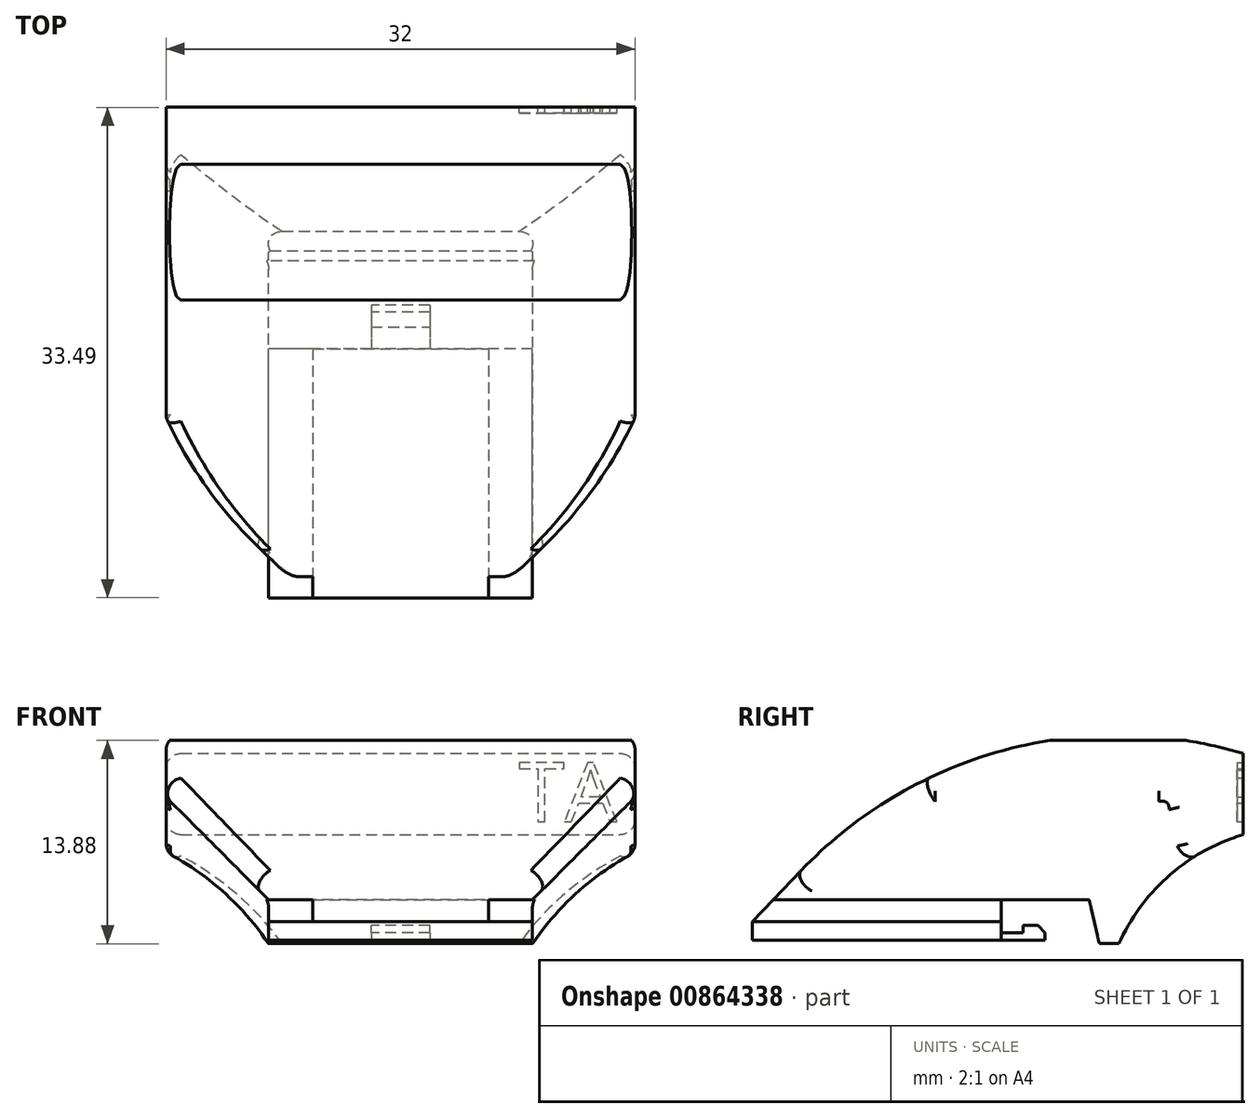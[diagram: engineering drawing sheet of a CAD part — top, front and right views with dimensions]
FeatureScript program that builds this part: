
annotation { "Feature Type Name" : "Feature", "Feature Type Description" : "" }
export const myFeature = defineFeature(function(context is Context, id is Id, definition is map)
    precondition{}
    {
        {
            var Q0;
            Q0=qCreatedBy(makeId("Front.planeOp"),FACE);
            var sketch = newSketch(context, id + "F0", { "sketchPlane" : qUnion([Q0])});
            skLineSegment(sketch, "E0.bottom", {"start": v(9, 0.63) * mm, "end": v(-9, 0.63) * mm});
            skLineSegment(sketch, "E0.top", {"start": v(9, -0.62) * mm, "end": v(-9, -0.62) * mm});
            skLineSegment(sketch, "E0.left", {"start": v(9, 0.63) * mm, "end": v(9, -0.62) * mm});
            skLineSegment(sketch, "E0.right", {"start": v(-9, 0.63) * mm, "end": v(-9, -0.62) * mm});
            skPoint(sketch, "E0.middle", {"position": v(0, 0) * mm});
            skSolve(sketch);
        }
        {
            var Q0;
            Q0=makeQuery(id+"F0.imprint","IMPRINT",FACE,{"disambiguationData":[TD([[makeQuery(id+"F0.imprint","IMPRINT",EDGE,{"derivedFrom":sQuery(id+"F0.wireOp",EDGE,"E0.bottom")}),1.0]])]});
            extrude(context, id + "F1", {"entities" : qUnion([Q0]), "depth" : 17 * mm, "offsetDistance" : 25 * mm});
        }
        {
            var Q0;
            Q0=makeQuery(id+"F1.opExtrude","SWEPT_FACE",FACE,{"disambiguationData":[OSD([sQuery(id+"F0.wireOp",EDGE,"E0.bottom")])]});
            var sketch = newSketch(context, id + "F2", { "sketchPlane" : qUnion([Q0])});
            skLineSegment(sketch, "E1", {"start": v(-9, 0) * mm, "end": v(-6, 0) * mm});
            skLineSegment(sketch, "E2", {"start": v(9, 0) * mm, "end": v(6, 0) * mm});
            skLineSegment(sketch, "E3", {"start": v(-6, 0) * mm, "end": v(-6, -17) * mm});
            skLineSegment(sketch, "E4", {"start": v(6, 0) * mm, "end": v(6, -17) * mm});
            skSolve(sketch);
        }
        {
            var Q0;
            {var subQ0=sQuery(id+"F2.wireOp",EDGE,"E3");Q0=makeQuery(id+"F2.imprint","IMPRINT",FACE,{"disambiguationData":[TD([[makeQuery(id+"F2.imprint","IMPRINT",EDGE,{"derivedFrom":subQ0}),1.0]])]});}
            extrude(context, id + "F3", {"entities" : qUnion([Q0]), "operationType" : NewBodyOperationType.ADD, "depth" : 1.5 * mm, "offsetDistance" : 25 * mm});
        }
        {
            var Q0;
            {var subQ0=sQuery(id+"F0.wireOp",EDGE,"E0.bottom");var subQ1=makeQuery(id+"F1.opExtrude","CAP_EDGE",EDGE,{"disambiguationData":[OSD([subQ0])],"isStart":true});Q0=makeQuery(id+"F3.boolean.opBoolean","MERGE",FACE,{"derivedFrom":[makeQuery(id+"F1.opExtrude","CAP_FACE",FACE,{"disambiguationData":[OSD([subQ0,sQuery(id+"F0.wireOp",EDGE,"E0.top"),sQuery(id+"F0.wireOp",EDGE,"E0.left"),sQuery(id+"F0.wireOp",EDGE,"E0.right")])],"isStart":true}),makeQuery(id+"F3.opExtrude","SWEPT_FACE",FACE,{"disambiguationData":[OSD([subQ0]),TDD([makeQuery(id+"F2.imprint","IMPRINT",EDGE,{"disambiguationData":[TD([[makeQuery(id+"F2.imprint","INTERSECT",VERTEX,{"derivedFrom":[subQ1,sQuery(id+"F2.wireOp",EDGE,"E1"),sQuery(id+"F2.wireOp",EDGE,"E3")]}),1.0]])],"derivedFrom":subQ1})])]})]});}
            var sketch = newSketch(context, id + "F4", { "sketchPlane" : qUnion([Q0])});
            skLineSegment(sketch, "E5", {"start": v(-9, -0.62) * mm, "end": v(0, -0.62) * mm});
            skLineSegment(sketch, "E6", {"start": v(-2, 0.38) * mm, "end": v(-2, -0.62) * mm});
            skLineSegment(sketch, "E7", {"start": v(2, 0.38) * mm, "end": v(2, -0.62) * mm});
            skLineSegment(sketch, "E8", {"start": v(-2, 0.38) * mm, "end": v(2, 0.38) * mm});
            skSolve(sketch);
        }
        {
            var Q0;
            {var subQ1=sQuery(id+"F4.wireOp",EDGE,"E6");Q0=makeQuery(id+"F4.imprint","IMPRINT",FACE,{"disambiguationData":[TD([[makeQuery(id+"F4.imprint","IMPRINT",EDGE,{"derivedFrom":subQ1}),1.0]])]});}
            extrude(context, id + "F5", {"entities" : qUnion([Q0]), "operationType" : NewBodyOperationType.ADD, "depth" : 3 * mm, "offsetDistance" : 25 * mm});
        }
        {
            var Q0;
            Q0=makeQuery(id+"F5.opExtrude","SWEPT_FACE",FACE,{"disambiguationData":[OSD([sQuery(id+"F4.wireOp",EDGE,"E8")])]});
            var sketch = newSketch(context, id + "F6", { "sketchPlane" : qUnion([Q0])});
            skLineSegment(sketch, "E9", {"start": v(-2, 1.5) * mm, "end": v(2, 1.5) * mm});
            skSolve(sketch);
        }
        {
            var Q0;
            {var subQ0=sQuery(id+"F6.wireOp",EDGE,"E9");Q0=makeQuery(id+"F6.imprint","IMPRINT",FACE,{"disambiguationData":[TD([[makeQuery(id+"F6.imprint","IMPRINT",EDGE,{"derivedFrom":subQ0}),-1.0]])]});}
            extrude(context, id + "F7", {"entities" : qUnion([Q0]), "operationType" : NewBodyOperationType.REMOVE, "oppositeDirection" : true, "depth" : .5 * mm, "offsetDistance" : 25 * mm});
        }
        {
            var Q0;
            Q0=makeQuery(id+"F5.opExtrude","SWEPT_FACE",FACE,{"disambiguationData":[OSD([sQuery(id+"F4.wireOp",EDGE,"E7")])]});
            var sketch = newSketch(context, id + "F8", { "sketchPlane" : qUnion([Q0])});
            skLineSegment(sketch, "E10", {"start": v(-1.5, -0.12) * mm, "end": v(-3, -0.12) * mm});
            skLineSegment(sketch, "E11", {"start": v(-1.5, 0.38) * mm, "end": v(-2.5, 0.38) * mm});
            skLineSegment(sketch, "E12", {"start": v(-3, -0.12) * mm, "end": v(-2.5, 0.38) * mm});
            skSolve(sketch);
        }
        {
            var Q0;
            {var subQ0=sQuery(id+"F8.wireOp",EDGE,"E12");Q0=makeQuery(id+"F8.imprint","IMPRINT",FACE,{"disambiguationData":[TD([[makeQuery(id+"F8.imprint","IMPRINT",EDGE,{"derivedFrom":subQ0}),1.0]])]});}
            extrude(context, id + "F9", {"entities" : qUnion([Q0]), "operationType" : NewBodyOperationType.REMOVE, "oppositeDirection" : true, "depth" : 25 * mm, "offsetDistance" : 25 * mm});
        }
        {
            var Q0;
            Q0=makeQuery(id+"F3.opExtrude","CAP_FACE",FACE,{"disambiguationData":[OSD([sQuery(id+"F0.wireOp",EDGE,"E0.bottom"),sQuery(id+"F2.wireOp",EDGE,"E3"),sQuery(id+"F2.wireOp",EDGE,"E4")])],"isStart":false});
            var sketch = newSketch(context, id + "F10", { "sketchPlane" : qUnion([Q0])});
            skLineSegment(sketch, "E13", {"start": v(0, 0) * mm, "end": v(0, -17) * mm});
            skSolve(sketch);
        }
        {
            var Q0;
            {var subQ4=sQuery(id+"F10.wireOp",EDGE,"9KFDr5Zl-xlse-Ylvu-UwML-SPBPVxaVvAoh");Q0=makeQuery(id+"F10.imprint","IMPRINT",FACE,{"disambiguationData":[TD([[makeQuery(id+"F10.imprint","IMPRINT",EDGE,{"derivedFrom":subQ4}),-1.0]])]});}
            var Q1;
            {var subQ4=sQuery(id+"F10.wireOp",EDGE,"uYcF2vPk-5izG-vbNe-kog8-wCf3jsevN1tl");Q1=makeQuery(id+"F10.imprint","IMPRINT",FACE,{"disambiguationData":[TD([[makeQuery(id+"F10.imprint","IMPRINT",EDGE,{"derivedFrom":subQ4}),-1.0]])]});}
            var Q2;
            {var subQ1=sQuery(id+"F10.wireOp",EDGE,"418b0c24-5611-44d3-8d25-239d1beeb747.sketch_text.stroke-0");Q2=makeQuery(id+"F10.imprint","IMPRINT",FACE,{"disambiguationData":[TD([[makeQuery(id+"F10.imprint","IMPRINT",EDGE,{"derivedFrom":subQ1}),-1.0]])]});}
            var Q3;
            Q3=makeQuery(id+"F10.imprint","IMPRINT",FACE,{"disambiguationData":[TD([[makeQuery(id+"F10.imprint","IMPRINT",EDGE,{"derivedFrom":sQuery(id+"F10.wireOp",EDGE,"418b0c24-5611-44d3-8d25-239d1beeb747.sketch_text.stroke-13")}),-1.0]])]});
            var Q4;
            {var subQ0=sQuery(id+"F10.wireOp",EDGE,"418b0c24-5611-44d3-8d25-239d1beeb747.sketch_text.stroke-6");var subQ1=sQuery(id+"F10.wireOp",EDGE,"E13");var subQ2=makeQuery(id+"F10.imprint","INTERSECT",VERTEX,{"derivedFrom":[subQ1,subQ0]});Q4=makeQuery(id+"F10.imprint","IMPRINT",FACE,{"disambiguationData":[TD([[makeQuery(id+"F10.imprint","IMPRINT",EDGE,{"disambiguationData":[TD([[subQ2,-1.0]])],"derivedFrom":subQ1}),1.0]])]});}
            extrude(context, id + "F11", {"entities" : qUnion([Q0, Q1, Q2, Q3, Q4]), "operationType" : NewBodyOperationType.REMOVE, "oppositeDirection" : true, "depth" : .4 * mm, "offsetDistance" : 25 * mm});
        }
        {
            var Q0;
            {var subQ0=sQuery(id+"F10.wireOp",EDGE,"E13");Q0=makeQuery(id+"F10.imprint","IMPRINT",FACE,{"disambiguationData":[TD([[makeQuery(id+"F10.imprint","IMPRINT",EDGE,{"derivedFrom":subQ0}),-1.0]])]});}
            var Q1;
            {var subQ0=sQuery(id+"F10.wireOp",EDGE,"E13");Q1=makeQuery(id+"F10.imprint","IMPRINT",FACE,{"disambiguationData":[TD([[makeQuery(id+"F10.imprint","IMPRINT",EDGE,{"derivedFrom":subQ0}),1.0]])]});}
            var Q2;
            Q2=makeQuery(id+"F11.boolean.opBoolean","COPY",FACE,{"derivedFrom":makeQuery(id+"F11.opExtrude","CAP_FACE",FACE,{"disambiguationData":[OSD([sQuery(id+"F0.wireOp",EDGE,"E0.bottom"),sQuery(id+"F2.wireOp",EDGE,"E4"),sQuery(id+"F10.wireOp",EDGE,"E13")])],"isStart":false})});
            extrude(context, id + "F12", {"entities" : qUnion([Q0, Q1, Q2]), "operationType" : NewBodyOperationType.ADD, "depth" : 2 * mm, "offsetDistance" : 25 * mm});
        }
        {
            var Q0;
            {var subQ0=sQuery(id+"F2.wireOp",EDGE,"E3");Q0=makeQuery(id+"F12.boolean.opBoolean","MERGE",FACE,{"derivedFrom":[makeQuery(id+"F3.opExtrude","SWEPT_FACE",FACE,{"disambiguationData":[OSD([subQ0])]}),makeQuery(id+"F12.opExtrude","SWEPT_FACE",FACE,{"disambiguationData":[OSD([subQ0])]})]});}
            var sketch = newSketch(context, id + "F13", { "sketchPlane" : qUnion([Q0])});
            skLineSegment(sketch, "E14", {"start": v(13.65, 4.13) * mm, "end": v(17, 0.63) * mm});
            skSolve(sketch);
        }
        {
            var Q0;
            {var subQ0=sQuery(id+"F13.wireOp",EDGE,"E14");Q0=makeQuery(id+"F13.imprint","IMPRINT",FACE,{"disambiguationData":[TD([[makeQuery(id+"F13.imprint","IMPRINT",EDGE,{"derivedFrom":subQ0}),1.0]])]});}
            extrude(context, id + "F14", {"entities" : qUnion([Q0]), "operationType" : NewBodyOperationType.REMOVE, "oppositeDirection" : true, "depth" : 25 * mm, "offsetDistance" : 25 * mm});
        }
        {
            var Q0;
            {var subQ0=sQuery(id+"F2.wireOp",EDGE,"E3");var subQ1=sQuery(id+"F0.wireOp",EDGE,"E0.bottom");var subQ2=makeQuery(id+"F1.opExtrude","CAP_EDGE",EDGE,{"disambiguationData":[OSD([subQ1])],"isStart":true});var subQ3=sQuery(id+"F2.wireOp",EDGE,"E4");var subQ4=makeQuery(id+"F2.imprint","IMPRINT",EDGE,{"disambiguationData":[TD([[makeQuery(id+"F2.imprint","INTERSECT",VERTEX,{"derivedFrom":[subQ2,sQuery(id+"F2.wireOp",EDGE,"E1"),subQ0]}),1.0]])],"derivedFrom":subQ2});var subQ5=makeQuery(id+"F3.opExtrude","CAP_EDGE",EDGE,{"disambiguationData":[OSD([subQ1]),TDD([subQ4])],"isStart":false});var subQ7=makeQuery(id+"F10.imprint","IMPRINT",EDGE,{"disambiguationData":[TD([[makeQuery(id+"F10.imprint","INTERSECT",VERTEX,{"derivedFrom":[makeQuery(id+"F3.opExtrude","CAP_EDGE",EDGE,{"disambiguationData":[OSD([subQ3])],"isStart":false}),subQ5]}),-1.0]])],"derivedFrom":subQ5});Q0=makeQuery(id+"F12.boolean.opBoolean","MERGE",FACE,{"derivedFrom":[makeQuery(id+"F7.boolean.opBoolean","MERGE",FACE,{"derivedFrom":[makeQuery(id+"F3.boolean.opBoolean","MERGE",FACE,{"derivedFrom":[makeQuery(id+"F1.opExtrude","CAP_FACE",FACE,{"disambiguationData":[OSD([subQ1,sQuery(id+"F0.wireOp",EDGE,"E0.top"),sQuery(id+"F0.wireOp",EDGE,"E0.left"),sQuery(id+"F0.wireOp",EDGE,"E0.right")])],"isStart":true}),makeQuery(id+"F3.opExtrude","SWEPT_FACE",FACE,{"disambiguationData":[OSD([subQ1]),TDD([subQ4])]})]}),makeQuery(id+"F7.opExtrude","SWEPT_FACE",FACE,{"disambiguationData":[OSD([sQuery(id+"F4.wireOp",EDGE,"E8")])]})]}),makeQuery(id+"F12.opExtrude","SWEPT_FACE",FACE,{"disambiguationData":[OSD([subQ1]),TDD([makeQuery(id+"F10.imprint","IMPRINT",EDGE,{"disambiguationData":[TD([[makeQuery(id+"F10.imprint","INTERSECT",VERTEX,{"derivedFrom":[makeQuery(id+"F3.opExtrude","CAP_EDGE",EDGE,{"disambiguationData":[OSD([subQ0])],"isStart":false}),subQ5]}),1.0]])],"derivedFrom":subQ5}),subQ7])]}),makeQuery(id+"F12.opExtrude","SWEPT_FACE",FACE,{"disambiguationData":[OSD([subQ1]),TDD([makeQuery(id+"F11.boolean.opBoolean","COPY",EDGE,{"derivedFrom":makeQuery(id+"F11.opExtrude","CAP_EDGE",EDGE,{"disambiguationData":[OSD([subQ1]),TDD([subQ7])],"isStart":false})})])]})]});}
            var sketch = newSketch(context, id + "F15", { "sketchPlane" : qUnion([Q0])});
            skLineSegment(sketch, "E15", {"start": v(6, 4.13) * mm, "end": v(6, 2.13) * mm});
            skLineSegment(sketch, "E16", {"start": v(6, 2.13) * mm, "end": v(-6, 2.13) * mm});
            skSolve(sketch);
        }
        {
            var Q0;
            Q0=makeQuery(id+"F15.imprint","IMPRINT",FACE,{"disambiguationData":[TD([[makeQuery(id+"F15.imprint","IMPRINT",EDGE,{"derivedFrom":sQuery(id+"F15.wireOp",EDGE,"E15")}),-1.0]])]});
            extrude(context, id + "F16", {"entities" : qUnion([Q0]), "operationType" : NewBodyOperationType.ADD, "depth" : 8 * mm, "offsetDistance" : 25 * mm});
        }
        {
            var Q0;
            Q0=makeQuery(id+"F16.opExtrude","SWEPT_FACE",FACE,{"disambiguationData":[OSD([sQuery(id+"F15.wireOp",EDGE,"E16")])]});
            var sketch = newSketch(context, id + "F17", { "sketchPlane" : qUnion([Q0])});
            skLineSegment(sketch, "E17", {"start": v(6, -8) * mm, "end": v(6, -6) * mm});
            skLineSegment(sketch, "E18", {"start": v(6, -6) * mm, "end": v(-6, -6) * mm});
            skSolve(sketch);
        }
        {
            var Q0;
            Q0=makeQuery(id+"F17.imprint","IMPRINT",FACE,{"disambiguationData":[TD([[makeQuery(id+"F17.imprint","IMPRINT",EDGE,{"derivedFrom":sQuery(id+"F17.wireOp",EDGE,"E17")}),1.0]])]});
            extrude(context, id + "F18", {"entities" : qUnion([Q0]), "operationType" : NewBodyOperationType.ADD, "depth" : 3 * mm, "offsetDistance" : 25 * mm});
        }
        {
            var Q0;
            {var subQ0=sQuery(id+"F2.wireOp",EDGE,"E4");Q0=makeQuery(id+"F18.boolean.opBoolean","MERGE",FACE,{"derivedFrom":[makeQuery(id+"F16.boolean.opBoolean","MERGE",FACE,{"derivedFrom":[makeQuery(id+"F12.boolean.opBoolean","MERGE",FACE,{"derivedFrom":[makeQuery(id+"F3.opExtrude","SWEPT_FACE",FACE,{"disambiguationData":[OSD([subQ0])]}),makeQuery(id+"F12.opExtrude","SWEPT_FACE",FACE,{"disambiguationData":[OSD([subQ0]),TDD([makeQuery(id+"F10.imprint","IMPRINT",EDGE,{"derivedFrom":makeQuery(id+"F3.opExtrude","CAP_EDGE",EDGE,{"disambiguationData":[OSD([subQ0])],"isStart":false})})])]}),makeQuery(id+"F12.opExtrude","SWEPT_FACE",FACE,{"disambiguationData":[OSD([subQ0]),TDD([makeQuery(id+"F11.boolean.opBoolean","COPY",EDGE,{"derivedFrom":makeQuery(id+"F11.opExtrude","CAP_EDGE",EDGE,{"disambiguationData":[OSD([subQ0])],"isStart":false})})])]})]}),makeQuery(id+"F16.opExtrude","SWEPT_FACE",FACE,{"disambiguationData":[OSD([sQuery(id+"F0.wireOp",EDGE,"E0.bottom"),sQuery(id+"F2.wireOp",EDGE,"E2"),subQ0])]})]}),makeQuery(id+"F18.opExtrude","SWEPT_FACE",FACE,{"disambiguationData":[OSD([sQuery(id+"F17.wireOp",EDGE,"E17")])]})]});}
            var sketch = newSketch(context, id + "F19", { "sketchPlane" : qUnion([Q0])});
            skLineSegment(sketch, "E19", {"start": v(6, 2.13) * mm, "end": v(6.7, -0.87) * mm});
            skSolve(sketch);
        }
        {
            var Q0;
            {var subQ0=sQuery(id+"F19.wireOp",EDGE,"E19");Q0=makeQuery(id+"F19.imprint","IMPRINT",FACE,{"disambiguationData":[TD([[makeQuery(id+"F19.imprint","IMPRINT",EDGE,{"derivedFrom":subQ0}),-1.0]])]});}
            extrude(context, id + "F20", {"entities" : qUnion([Q0]), "operationType" : NewBodyOperationType.REMOVE, "oppositeDirection" : true, "depth" : 25 * mm, "offsetDistance" : 25 * mm});
        }
        {
            var Q0;
            {var subQ0=sQuery(id+"F0.wireOp",EDGE,"E0.bottom");Q0=makeQuery(id+"F16.boolean.opBoolean","MERGE",FACE,{"derivedFrom":[makeQuery(id+"F12.opExtrude","CAP_FACE",FACE,{"disambiguationData":[OSD([subQ0,sQuery(id+"F2.wireOp",EDGE,"E3"),sQuery(id+"F2.wireOp",EDGE,"E4")])],"isStart":false}),makeQuery(id+"F16.opExtrude","SWEPT_FACE",FACE,{"disambiguationData":[OSD([subQ0])]})]});}
            extrude(context, id + "F21", {"entities" : qUnion([Q0]), "operationType" : NewBodyOperationType.ADD, "depth" : 25 * mm, "offsetDistance" : 25 * mm});
        }
        {
            var Q0;
            {var subQ0=sQuery(id+"F0.wireOp",EDGE,"E0.bottom");var subQ1=sQuery(id+"F15.wireOp",EDGE,"E16");Q0=makeQuery(id+"F21.boolean.opBoolean","MERGE",FACE,{"derivedFrom":[makeQuery(id+"F18.boolean.opBoolean","MERGE",FACE,{"derivedFrom":[makeQuery(id+"F16.opExtrude","CAP_FACE",FACE,{"disambiguationData":[OSD([subQ0,sQuery(id+"F2.wireOp",EDGE,"E2"),sQuery(id+"F2.wireOp",EDGE,"E4"),sQuery(id+"F15.wireOp",EDGE,"E15"),subQ1])],"isStart":false}),makeQuery(id+"F18.opExtrude","SWEPT_FACE",FACE,{"disambiguationData":[OSD([subQ1])]})]}),makeQuery(id+"F21.opExtrude","SWEPT_FACE",FACE,{"disambiguationData":[OSD([subQ0])]})]});}
            extrude(context, id + "F22", {"entities" : qUnion([Q0]), "operationType" : NewBodyOperationType.ADD, "depth" : 25 * mm, "offsetDistance" : 25 * mm});
        }
        {
            var Q0;
            {var subQ0=sQuery(id+"F17.wireOp",EDGE,"E17");var subQ1=sQuery(id+"F2.wireOp",EDGE,"E4");var subQ2=sQuery(id+"F2.wireOp",EDGE,"E2");var subQ3=sQuery(id+"F0.wireOp",EDGE,"E0.bottom");Q0=makeQuery(id+"F22.boolean.opBoolean","MERGE",FACE,{"derivedFrom":[makeQuery(id+"F21.boolean.opBoolean","MERGE",FACE,{"derivedFrom":[makeQuery(id+"F18.boolean.opBoolean","MERGE",FACE,{"derivedFrom":[makeQuery(id+"F16.boolean.opBoolean","MERGE",FACE,{"derivedFrom":[makeQuery(id+"F12.boolean.opBoolean","MERGE",FACE,{"derivedFrom":[makeQuery(id+"F3.opExtrude","SWEPT_FACE",FACE,{"disambiguationData":[OSD([subQ1])]}),makeQuery(id+"F12.opExtrude","SWEPT_FACE",FACE,{"disambiguationData":[OSD([subQ1]),TDD([makeQuery(id+"F10.imprint","IMPRINT",EDGE,{"derivedFrom":makeQuery(id+"F3.opExtrude","CAP_EDGE",EDGE,{"disambiguationData":[OSD([subQ1])],"isStart":false})})])]}),makeQuery(id+"F12.opExtrude","SWEPT_FACE",FACE,{"disambiguationData":[OSD([subQ1]),TDD([makeQuery(id+"F11.boolean.opBoolean","COPY",EDGE,{"derivedFrom":makeQuery(id+"F11.opExtrude","CAP_EDGE",EDGE,{"disambiguationData":[OSD([subQ1])],"isStart":false})})])]})]}),makeQuery(id+"F16.opExtrude","SWEPT_FACE",FACE,{"disambiguationData":[OSD([subQ3,subQ2,subQ1])]})]}),makeQuery(id+"F18.opExtrude","SWEPT_FACE",FACE,{"disambiguationData":[OSD([subQ0])]})]}),makeQuery(id+"F21.opExtrude","SWEPT_FACE",FACE,{"disambiguationData":[OSD([subQ3,subQ2,subQ1])]})]}),makeQuery(id+"F22.opExtrude","SWEPT_FACE",FACE,{"disambiguationData":[OSD([subQ3,subQ2,subQ1,sQuery(id+"F15.wireOp",EDGE,"E16"),subQ0])]})]});}
            var sketch = newSketch(context, id + "F23", { "sketchPlane" : qUnion([Q0])});
            skArc(sketch, "E20", {"start": v(33.44, -0.87) * mm, "mid": v(11.12, 13.2) * mm, "end": v(-13.65, 4.13) * mm});
            skLineSegment(sketch, "E21", {"start": v(16.5, -0.87) * mm, "end": v(16.5, 29.13) * mm});
            skArc(sketch, "E22", {"start": v(16.5, 6.57) * mm, "mid": v(11.45, 3.77) * mm, "end": v(8.03, -0.87) * mm});
            skSolve(sketch);
        }
        {
            var Q0;
            {var subQ4=sQuery(id+"F23.wireOp",EDGE,"E22");Q0=makeQuery(id+"F23.imprint","IMPRINT",FACE,{"disambiguationData":[TD([[makeQuery(id+"F23.imprint","IMPRINT",EDGE,{"derivedFrom":subQ4}),1.0]])]});}
            var Q1;
            {var subQ0=sQuery(id+"F23.wireOp",EDGE,"E21");var subQ1=makeQuery(id+"F23.imprint","INTERSECT",VERTEX,{"derivedFrom":[subQ0,sQuery(id+"F23.wireOp",EDGE,"E22")]});Q1=makeQuery(id+"F23.imprint","IMPRINT",FACE,{"disambiguationData":[TD([[makeQuery(id+"F23.imprint","IMPRINT",EDGE,{"disambiguationData":[TD([[subQ1,-1.0]])],"derivedFrom":subQ0}),-1.0]])]});}
            var Q2;
            {var subQ0=sQuery(id+"F23.wireOp",EDGE,"E21");var subQ1=sQuery(id+"F23.wireOp",EDGE,"E20");var subQ2=makeQuery(id+"F23.imprint","INTERSECT",VERTEX,{"derivedFrom":[subQ1,subQ0]});Q2=makeQuery(id+"F23.imprint","IMPRINT",FACE,{"disambiguationData":[TD([[makeQuery(id+"F23.imprint","IMPRINT",EDGE,{"disambiguationData":[TD([[subQ2,1.0]])],"derivedFrom":subQ1}),-1.0]])]});}
            var Q3;
            {var subQ1=sQuery(id+"F13.wireOp",EDGE,"E14");var subQ2=sQuery(id+"F2.wireOp",EDGE,"E4");var subQ3=makeQuery(id+"F21.opExtrude","SWEPT_EDGE",EDGE,{"disambiguationData":[OSD([subQ2,subQ1])]});Q3=makeQuery(id+"F23.imprint","IMPRINT",FACE,{"disambiguationData":[TD([[makeQuery(id+"F23.imprint","IMPRINT",EDGE,{"derivedFrom":subQ3}),1.0]])]});}
            extrude(context, id + "F24", {"entities" : qUnion([Q0, Q1, Q2, Q3]), "operationType" : NewBodyOperationType.REMOVE, "oppositeDirection" : true, "depth" : 25 * mm, "offsetDistance" : 25 * mm});
        }
        {
            var Q0;
            {var subQ0=sQuery(id+"F17.wireOp",EDGE,"E17");var subQ1=sQuery(id+"F2.wireOp",EDGE,"E4");var subQ2=sQuery(id+"F2.wireOp",EDGE,"E2");var subQ3=sQuery(id+"F0.wireOp",EDGE,"E0.bottom");Q0=makeQuery(id+"F22.boolean.opBoolean","MERGE",FACE,{"derivedFrom":[makeQuery(id+"F21.boolean.opBoolean","MERGE",FACE,{"derivedFrom":[makeQuery(id+"F18.boolean.opBoolean","MERGE",FACE,{"derivedFrom":[makeQuery(id+"F16.boolean.opBoolean","MERGE",FACE,{"derivedFrom":[makeQuery(id+"F12.boolean.opBoolean","MERGE",FACE,{"derivedFrom":[makeQuery(id+"F3.opExtrude","SWEPT_FACE",FACE,{"disambiguationData":[OSD([subQ1])]}),makeQuery(id+"F12.opExtrude","SWEPT_FACE",FACE,{"disambiguationData":[OSD([subQ1]),TDD([makeQuery(id+"F10.imprint","IMPRINT",EDGE,{"derivedFrom":makeQuery(id+"F3.opExtrude","CAP_EDGE",EDGE,{"disambiguationData":[OSD([subQ1])],"isStart":false})})])]}),makeQuery(id+"F12.opExtrude","SWEPT_FACE",FACE,{"disambiguationData":[OSD([subQ1]),TDD([makeQuery(id+"F11.boolean.opBoolean","COPY",EDGE,{"derivedFrom":makeQuery(id+"F11.opExtrude","CAP_EDGE",EDGE,{"disambiguationData":[OSD([subQ1])],"isStart":false})})])]})]}),makeQuery(id+"F16.opExtrude","SWEPT_FACE",FACE,{"disambiguationData":[OSD([subQ3,subQ2,subQ1])]})]}),makeQuery(id+"F18.opExtrude","SWEPT_FACE",FACE,{"disambiguationData":[OSD([subQ0])]})]}),makeQuery(id+"F21.opExtrude","SWEPT_FACE",FACE,{"disambiguationData":[OSD([subQ3,subQ2,subQ1])]})]}),makeQuery(id+"F22.opExtrude","SWEPT_FACE",FACE,{"disambiguationData":[OSD([subQ3,subQ2,subQ1,sQuery(id+"F15.wireOp",EDGE,"E16"),subQ0])]})]});}
            var sketch = newSketch(context, id + "F25", { "sketchPlane" : qUnion([Q0])});
            skLineSegment(sketch, "E23", {"start": v(0, 2.13) * mm, "end": v(-15.57, 2.13) * mm});
            skSolve(sketch);
        }
        {
            var Q0;
            {var subQ0=sQuery(id+"F15.wireOp",EDGE,"E16");var subQ1=sQuery(id+"F15.wireOp",EDGE,"E15");var subQ2=sQuery(id+"F2.wireOp",EDGE,"E3");var subQ3=sQuery(id+"F2.wireOp",EDGE,"E1");var subQ4=sQuery(id+"F0.wireOp",EDGE,"E0.bottom");Q0=makeQuery(id+"F22.boolean.opBoolean","MERGE",FACE,{"derivedFrom":[makeQuery(id+"F21.boolean.opBoolean","MERGE",FACE,{"derivedFrom":[makeQuery(id+"F18.boolean.opBoolean","MERGE",FACE,{"derivedFrom":[makeQuery(id+"F16.boolean.opBoolean","MERGE",FACE,{"derivedFrom":[makeQuery(id+"F12.boolean.opBoolean","MERGE",FACE,{"derivedFrom":[makeQuery(id+"F3.opExtrude","SWEPT_FACE",FACE,{"disambiguationData":[OSD([subQ2])]}),makeQuery(id+"F12.opExtrude","SWEPT_FACE",FACE,{"disambiguationData":[OSD([subQ2])]})]}),makeQuery(id+"F16.opExtrude","SWEPT_FACE",FACE,{"disambiguationData":[OSD([subQ1])]})]}),makeQuery(id+"F18.opExtrude","SWEPT_FACE",FACE,{"disambiguationData":[OSD([subQ4,subQ3,subQ2,subQ1,subQ0])]})]}),makeQuery(id+"F21.opExtrude","SWEPT_FACE",FACE,{"disambiguationData":[OSD([subQ4,subQ2,subQ1])]})]}),makeQuery(id+"F22.opExtrude","SWEPT_FACE",FACE,{"disambiguationData":[OSD([subQ4,subQ3,subQ2,subQ1,subQ0])]})]});}
            var sketch = newSketch(context, id + "F26", { "sketchPlane" : qUnion([Q0])});
            skLineSegment(sketch, "E24", {"start": v(0, 2.13) * mm, "end": v(15.57, 2.13) * mm});
            skSolve(sketch);
        }
        {
            var Q0;
            {var subQ3=sQuery(id+"F25.wireOp",EDGE,"E23");Q0=makeQuery(id+"F25.imprint","IMPRINT",FACE,{"disambiguationData":[TD([[makeQuery(id+"F25.imprint","IMPRINT",EDGE,{"derivedFrom":subQ3}),-1.0]])]});}
            extrude(context, id + "F27", {"entities" : qUnion([Q0]), "operationType" : NewBodyOperationType.ADD, "depth" : 10 * mm, "offsetDistance" : 25 * mm});
        }
        {
            var Q0;
            {var subQ6=sQuery(id+"F26.wireOp",EDGE,"E24");Q0=makeQuery(id+"F26.imprint","IMPRINT",FACE,{"disambiguationData":[TD([[makeQuery(id+"F26.imprint","IMPRINT",EDGE,{"derivedFrom":subQ6}),1.0]])]});}
            var sketch = newSketch(context, id + "F28", { "sketchPlane" : qUnion([Q0])});
            skSolve(sketch);
        }
        {
            var Q0;
            {var subQ6=sQuery(id+"F26.wireOp",EDGE,"E24");Q0=makeQuery(id+"F28.imprint","IMPRINT",FACE,{"disambiguationData":[TD([[makeQuery(id+"F28.imprint","IMPRINT",EDGE,{"derivedFrom":makeQuery(id+"F26.imprint","IMPRINT",EDGE,{"derivedFrom":subQ6})}),1.0]])]});}
            extrude(context, id + "F29", {"entities" : qUnion([Q0]), "operationType" : NewBodyOperationType.ADD, "depth" : 10 * mm, "offsetDistance" : 25 * mm});
        }
        {
            var Q0;
            Q0=makeQuery(id+"F29.opExtrude","CAP_EDGE",EDGE,{"disambiguationData":[OSD([sQuery(id+"F0.wireOp",EDGE,"E0.bottom"),sQuery(id+"F2.wireOp",EDGE,"E1"),sQuery(id+"F2.wireOp",EDGE,"E3"),sQuery(id+"F15.wireOp",EDGE,"E15"),sQuery(id+"F15.wireOp",EDGE,"E16"),sQuery(id+"F26.wireOp",EDGE,"E24")])],"isStart":false});
            var Q1;
            Q1=makeQuery(id+"F29.opExtrude","CAP_EDGE",EDGE,{"disambiguationData":[OSD([sQuery(id+"F0.wireOp",EDGE,"E0.bottom"),sQuery(id+"F2.wireOp",EDGE,"E1"),sQuery(id+"F2.wireOp",EDGE,"E3"),sQuery(id+"F15.wireOp",EDGE,"E15"),sQuery(id+"F15.wireOp",EDGE,"E16"),sQuery(id+"F19.wireOp",EDGE,"E19")])],"isStart":false});
            var Q2;
            Q2=makeQuery(id+"F27.opExtrude","CAP_EDGE",EDGE,{"disambiguationData":[OSD([sQuery(id+"F19.wireOp",EDGE,"E19")])],"isStart":false});
            var Q3;
            Q3=makeQuery(id+"F27.opExtrude","CAP_EDGE",EDGE,{"disambiguationData":[OSD([sQuery(id+"F0.wireOp",EDGE,"E0.bottom"),sQuery(id+"F2.wireOp",EDGE,"E2"),sQuery(id+"F2.wireOp",EDGE,"E4"),sQuery(id+"F15.wireOp",EDGE,"E16"),sQuery(id+"F25.wireOp",EDGE,"E23")])],"isStart":false});
            chamfer(context, id + "F30", {"entities" : qUnion([Q0, Q1, Q2, Q3]), "width" : 7 * mm, "tangentPropagation" : true});
        }
        {
            var Q0;
            {var subQ0=sQuery(id+"F25.wireOp",EDGE,"E23");var subQ1=sQuery(id+"F15.wireOp",EDGE,"E16");var subQ2=sQuery(id+"F2.wireOp",EDGE,"E4");var subQ3=sQuery(id+"F2.wireOp",EDGE,"E2");var subQ4=sQuery(id+"F0.wireOp",EDGE,"E0.bottom");Q0=makeQuery(id+"F30.opChamfer","BLEND_EDGE",EDGE,{"blendedFrom":[makeQuery(id+"F27.opExtrude","CAP_EDGE",EDGE,{"disambiguationData":[OSD([subQ4,subQ3,subQ2,subQ1,subQ0])],"isStart":false}),makeQuery(id+"F27.opExtrude","CAP_FACE",FACE,{"disambiguationData":[OSD([subQ4,subQ3,subQ2,sQuery(id+"F13.wireOp",EDGE,"E14"),subQ1,sQuery(id+"F17.wireOp",EDGE,"E17"),sQuery(id+"F19.wireOp",EDGE,"E19"),sQuery(id+"F23.wireOp",EDGE,"E20"),sQuery(id+"F23.wireOp",EDGE,"E21"),sQuery(id+"F23.wireOp",EDGE,"E22"),subQ0])],"isStart":false})],"blendedInto":[makeQuery(id+"F27.opExtrude","CAP_FACE",FACE,{"disambiguationData":[OSD([subQ4,subQ3,subQ2,sQuery(id+"F13.wireOp",EDGE,"E14"),subQ1,sQuery(id+"F17.wireOp",EDGE,"E17"),sQuery(id+"F19.wireOp",EDGE,"E19"),sQuery(id+"F23.wireOp",EDGE,"E20"),sQuery(id+"F23.wireOp",EDGE,"E21"),sQuery(id+"F23.wireOp",EDGE,"E22"),subQ0])],"isStart":false})]});}
            var Q1;
            {var subQ0=sQuery(id+"F19.wireOp",EDGE,"E19");Q1=makeQuery(id+"F30.opChamfer","BLEND_EDGE",EDGE,{"blendedFrom":[makeQuery(id+"F27.opExtrude","CAP_EDGE",EDGE,{"disambiguationData":[OSD([subQ0])],"isStart":false}),makeQuery(id+"F27.opExtrude","CAP_FACE",FACE,{"disambiguationData":[OSD([sQuery(id+"F0.wireOp",EDGE,"E0.bottom"),sQuery(id+"F2.wireOp",EDGE,"E2"),sQuery(id+"F2.wireOp",EDGE,"E4"),sQuery(id+"F13.wireOp",EDGE,"E14"),sQuery(id+"F15.wireOp",EDGE,"E16"),sQuery(id+"F17.wireOp",EDGE,"E17"),subQ0,sQuery(id+"F23.wireOp",EDGE,"E20"),sQuery(id+"F23.wireOp",EDGE,"E21"),sQuery(id+"F23.wireOp",EDGE,"E22"),sQuery(id+"F25.wireOp",EDGE,"E23")])],"isStart":false})],"blendedInto":[makeQuery(id+"F27.opExtrude","CAP_FACE",FACE,{"disambiguationData":[OSD([sQuery(id+"F0.wireOp",EDGE,"E0.bottom"),sQuery(id+"F2.wireOp",EDGE,"E2"),sQuery(id+"F2.wireOp",EDGE,"E4"),sQuery(id+"F13.wireOp",EDGE,"E14"),sQuery(id+"F15.wireOp",EDGE,"E16"),sQuery(id+"F17.wireOp",EDGE,"E17"),subQ0,sQuery(id+"F23.wireOp",EDGE,"E20"),sQuery(id+"F23.wireOp",EDGE,"E21"),sQuery(id+"F23.wireOp",EDGE,"E22"),sQuery(id+"F25.wireOp",EDGE,"E23")])],"isStart":false})]});}
            var Q2;
            Q2=makeQuery(id+"F30.opChamfer","BLEND_EDGE",EDGE,{"blendedFrom":[makeQuery(id+"F27.opExtrude","CAP_EDGE",EDGE,{"disambiguationData":[OSD([sQuery(id+"F0.wireOp",EDGE,"E0.bottom"),sQuery(id+"F2.wireOp",EDGE,"E2"),sQuery(id+"F2.wireOp",EDGE,"E4"),sQuery(id+"F15.wireOp",EDGE,"E16"),sQuery(id+"F25.wireOp",EDGE,"E23")])],"isStart":false}),makeQuery(id+"F27.opExtrude","CAP_EDGE",EDGE,{"disambiguationData":[OSD([sQuery(id+"F19.wireOp",EDGE,"E19")])],"isStart":false})],"blendedInto":[]});
            var Q3;
            {var subQ0=sQuery(id+"F23.wireOp",EDGE,"E22");Q3=makeQuery(id+"F30.opChamfer","BLEND_EDGE",EDGE,{"blendedFrom":[makeQuery(id+"F27.opExtrude","CAP_EDGE",EDGE,{"disambiguationData":[OSD([sQuery(id+"F19.wireOp",EDGE,"E19")])],"isStart":false}),makeQuery(id+"F29.boolean.opBoolean","MERGE",FACE,{"derivedFrom":[makeQuery(id+"F27.boolean.opBoolean","MERGE",FACE,{"derivedFrom":[makeQuery(id+"F24.boolean.opBoolean","COPY",FACE,{"derivedFrom":makeQuery(id+"F24.opExtrude","SWEPT_FACE",FACE,{"disambiguationData":[OSD([subQ0])]})}),makeQuery(id+"F27.opExtrude","SWEPT_FACE",FACE,{"disambiguationData":[OSD([subQ0])]})]}),makeQuery(id+"F29.opExtrude","SWEPT_FACE",FACE,{"disambiguationData":[OSD([sQuery(id+"F0.wireOp",EDGE,"E0.bottom"),sQuery(id+"F2.wireOp",EDGE,"E1"),sQuery(id+"F2.wireOp",EDGE,"E3"),sQuery(id+"F15.wireOp",EDGE,"E15"),sQuery(id+"F15.wireOp",EDGE,"E16"),subQ0])]})]})],"blendedInto":[makeQuery(id+"F29.boolean.opBoolean","MERGE",FACE,{"derivedFrom":[makeQuery(id+"F27.boolean.opBoolean","MERGE",FACE,{"derivedFrom":[makeQuery(id+"F24.boolean.opBoolean","COPY",FACE,{"derivedFrom":makeQuery(id+"F24.opExtrude","SWEPT_FACE",FACE,{"disambiguationData":[OSD([subQ0])]})}),makeQuery(id+"F27.opExtrude","SWEPT_FACE",FACE,{"disambiguationData":[OSD([subQ0])]})]}),makeQuery(id+"F29.opExtrude","SWEPT_FACE",FACE,{"disambiguationData":[OSD([sQuery(id+"F0.wireOp",EDGE,"E0.bottom"),sQuery(id+"F2.wireOp",EDGE,"E1"),sQuery(id+"F2.wireOp",EDGE,"E3"),sQuery(id+"F15.wireOp",EDGE,"E15"),sQuery(id+"F15.wireOp",EDGE,"E16"),subQ0])]})]})]});}
            var Q4;
            Q4=makeQuery(id+"F27.opExtrude","CAP_EDGE",EDGE,{"disambiguationData":[OSD([sQuery(id+"F23.wireOp",EDGE,"E22")])],"isStart":false});
            var Q5;
            {var subQ0=sQuery(id+"F15.wireOp",EDGE,"E16");var subQ1=sQuery(id+"F15.wireOp",EDGE,"E15");var subQ2=sQuery(id+"F2.wireOp",EDGE,"E3");var subQ3=sQuery(id+"F2.wireOp",EDGE,"E1");var subQ4=sQuery(id+"F0.wireOp",EDGE,"E0.bottom");Q5=makeQuery(id+"F30.opChamfer","BLEND_EDGE",EDGE,{"blendedFrom":[makeQuery(id+"F29.opExtrude","CAP_EDGE",EDGE,{"disambiguationData":[OSD([subQ4,subQ3,subQ2,subQ1,subQ0,sQuery(id+"F26.wireOp",EDGE,"E24")])],"isStart":false}),makeQuery(id+"F29.opExtrude","CAP_EDGE",EDGE,{"disambiguationData":[OSD([subQ4,subQ3,subQ2,subQ1,subQ0,sQuery(id+"F19.wireOp",EDGE,"E19")])],"isStart":false})],"blendedInto":[]});}
            var Q6;
            {var subQ0=sQuery(id+"F23.wireOp",EDGE,"E22");var subQ1=sQuery(id+"F15.wireOp",EDGE,"E16");var subQ2=sQuery(id+"F15.wireOp",EDGE,"E15");var subQ3=sQuery(id+"F2.wireOp",EDGE,"E3");var subQ4=sQuery(id+"F2.wireOp",EDGE,"E1");var subQ5=sQuery(id+"F0.wireOp",EDGE,"E0.bottom");Q6=makeQuery(id+"F30.opChamfer","BLEND_EDGE",EDGE,{"blendedFrom":[makeQuery(id+"F29.opExtrude","CAP_EDGE",EDGE,{"disambiguationData":[OSD([subQ5,subQ4,subQ3,subQ2,subQ1,sQuery(id+"F19.wireOp",EDGE,"E19")])],"isStart":false}),makeQuery(id+"F29.boolean.opBoolean","MERGE",FACE,{"derivedFrom":[makeQuery(id+"F27.boolean.opBoolean","MERGE",FACE,{"derivedFrom":[makeQuery(id+"F24.boolean.opBoolean","COPY",FACE,{"derivedFrom":makeQuery(id+"F24.opExtrude","SWEPT_FACE",FACE,{"disambiguationData":[OSD([subQ0])]})}),makeQuery(id+"F27.opExtrude","SWEPT_FACE",FACE,{"disambiguationData":[OSD([subQ0])]})]}),makeQuery(id+"F29.opExtrude","SWEPT_FACE",FACE,{"disambiguationData":[OSD([subQ5,subQ4,subQ3,subQ2,subQ1,subQ0])]})]})],"blendedInto":[makeQuery(id+"F29.boolean.opBoolean","MERGE",FACE,{"derivedFrom":[makeQuery(id+"F27.boolean.opBoolean","MERGE",FACE,{"derivedFrom":[makeQuery(id+"F24.boolean.opBoolean","COPY",FACE,{"derivedFrom":makeQuery(id+"F24.opExtrude","SWEPT_FACE",FACE,{"disambiguationData":[OSD([subQ0])]})}),makeQuery(id+"F27.opExtrude","SWEPT_FACE",FACE,{"disambiguationData":[OSD([subQ0])]})]}),makeQuery(id+"F29.opExtrude","SWEPT_FACE",FACE,{"disambiguationData":[OSD([subQ5,subQ4,subQ3,subQ2,subQ1,subQ0])]})]})]});}
            var Q7;
            Q7=makeQuery(id+"F29.opExtrude","CAP_EDGE",EDGE,{"disambiguationData":[OSD([sQuery(id+"F0.wireOp",EDGE,"E0.bottom"),sQuery(id+"F2.wireOp",EDGE,"E1"),sQuery(id+"F2.wireOp",EDGE,"E3"),sQuery(id+"F15.wireOp",EDGE,"E15"),sQuery(id+"F15.wireOp",EDGE,"E16"),sQuery(id+"F23.wireOp",EDGE,"E22")])],"isStart":false});
            var Q8;
            {var subQ0=sQuery(id+"F19.wireOp",EDGE,"E19");var subQ1=sQuery(id+"F15.wireOp",EDGE,"E16");var subQ2=sQuery(id+"F15.wireOp",EDGE,"E15");var subQ3=sQuery(id+"F2.wireOp",EDGE,"E3");var subQ4=sQuery(id+"F2.wireOp",EDGE,"E1");var subQ5=sQuery(id+"F0.wireOp",EDGE,"E0.bottom");Q8=makeQuery(id+"F30.opChamfer","BLEND_EDGE",EDGE,{"blendedFrom":[makeQuery(id+"F29.opExtrude","CAP_EDGE",EDGE,{"disambiguationData":[OSD([subQ5,subQ4,subQ3,subQ2,subQ1,subQ0])],"isStart":false}),makeQuery(id+"F29.opExtrude","CAP_FACE",FACE,{"disambiguationData":[OSD([subQ5,subQ4,subQ3,sQuery(id+"F13.wireOp",EDGE,"E14"),subQ2,subQ1,subQ0,sQuery(id+"F23.wireOp",EDGE,"E20"),sQuery(id+"F23.wireOp",EDGE,"E21"),sQuery(id+"F23.wireOp",EDGE,"E22"),sQuery(id+"F26.wireOp",EDGE,"E24")])],"isStart":false})],"blendedInto":[makeQuery(id+"F29.opExtrude","CAP_FACE",FACE,{"disambiguationData":[OSD([subQ5,subQ4,subQ3,sQuery(id+"F13.wireOp",EDGE,"E14"),subQ2,subQ1,subQ0,sQuery(id+"F23.wireOp",EDGE,"E20"),sQuery(id+"F23.wireOp",EDGE,"E21"),sQuery(id+"F23.wireOp",EDGE,"E22"),sQuery(id+"F26.wireOp",EDGE,"E24")])],"isStart":false})]});}
            var Q9;
            {var subQ0=sQuery(id+"F26.wireOp",EDGE,"E24");var subQ1=sQuery(id+"F15.wireOp",EDGE,"E16");var subQ2=sQuery(id+"F15.wireOp",EDGE,"E15");var subQ3=sQuery(id+"F2.wireOp",EDGE,"E3");var subQ4=sQuery(id+"F2.wireOp",EDGE,"E1");var subQ5=sQuery(id+"F0.wireOp",EDGE,"E0.bottom");Q9=makeQuery(id+"F30.opChamfer","BLEND_EDGE",EDGE,{"blendedFrom":[makeQuery(id+"F29.opExtrude","CAP_EDGE",EDGE,{"disambiguationData":[OSD([subQ5,subQ4,subQ3,subQ2,subQ1,subQ0])],"isStart":false}),makeQuery(id+"F29.opExtrude","CAP_FACE",FACE,{"disambiguationData":[OSD([subQ5,subQ4,subQ3,sQuery(id+"F13.wireOp",EDGE,"E14"),subQ2,subQ1,sQuery(id+"F19.wireOp",EDGE,"E19"),sQuery(id+"F23.wireOp",EDGE,"E20"),sQuery(id+"F23.wireOp",EDGE,"E21"),sQuery(id+"F23.wireOp",EDGE,"E22"),subQ0])],"isStart":false})],"blendedInto":[makeQuery(id+"F29.opExtrude","CAP_FACE",FACE,{"disambiguationData":[OSD([subQ5,subQ4,subQ3,sQuery(id+"F13.wireOp",EDGE,"E14"),subQ2,subQ1,sQuery(id+"F19.wireOp",EDGE,"E19"),sQuery(id+"F23.wireOp",EDGE,"E20"),sQuery(id+"F23.wireOp",EDGE,"E21"),sQuery(id+"F23.wireOp",EDGE,"E22"),subQ0])],"isStart":false})]});}
            var Q10;
            Q10=makeQuery(id+"F29.opExtrude","CAP_EDGE",EDGE,{"disambiguationData":[OSD([sQuery(id+"F0.wireOp",EDGE,"E0.bottom"),sQuery(id+"F2.wireOp",EDGE,"E1"),sQuery(id+"F2.wireOp",EDGE,"E3"),sQuery(id+"F15.wireOp",EDGE,"E15"),sQuery(id+"F15.wireOp",EDGE,"E16"),sQuery(id+"F23.wireOp",EDGE,"E20")])],"isStart":false});
            var Q11;
            {var subQ0=sQuery(id+"F23.wireOp",EDGE,"E20");var subQ1=sQuery(id+"F15.wireOp",EDGE,"E16");var subQ2=sQuery(id+"F15.wireOp",EDGE,"E15");var subQ3=sQuery(id+"F2.wireOp",EDGE,"E3");var subQ4=sQuery(id+"F2.wireOp",EDGE,"E1");var subQ5=sQuery(id+"F0.wireOp",EDGE,"E0.bottom");Q11=makeQuery(id+"F30.opChamfer","BLEND_EDGE",EDGE,{"blendedFrom":[makeQuery(id+"F29.opExtrude","CAP_EDGE",EDGE,{"disambiguationData":[OSD([subQ5,subQ4,subQ3,subQ2,subQ1,sQuery(id+"F26.wireOp",EDGE,"E24")])],"isStart":false}),makeQuery(id+"F29.boolean.opBoolean","MERGE",FACE,{"derivedFrom":[makeQuery(id+"F27.boolean.opBoolean","MERGE",FACE,{"derivedFrom":[makeQuery(id+"F24.boolean.opBoolean","COPY",FACE,{"derivedFrom":makeQuery(id+"F24.opExtrude","SWEPT_FACE",FACE,{"disambiguationData":[OSD([subQ0])]})}),makeQuery(id+"F27.opExtrude","SWEPT_FACE",FACE,{"disambiguationData":[OSD([subQ0])]})]}),makeQuery(id+"F29.opExtrude","SWEPT_FACE",FACE,{"disambiguationData":[OSD([subQ5,subQ4,subQ3,subQ2,subQ1,subQ0])]})]})],"blendedInto":[makeQuery(id+"F29.boolean.opBoolean","MERGE",FACE,{"derivedFrom":[makeQuery(id+"F27.boolean.opBoolean","MERGE",FACE,{"derivedFrom":[makeQuery(id+"F24.boolean.opBoolean","COPY",FACE,{"derivedFrom":makeQuery(id+"F24.opExtrude","SWEPT_FACE",FACE,{"disambiguationData":[OSD([subQ0])]})}),makeQuery(id+"F27.opExtrude","SWEPT_FACE",FACE,{"disambiguationData":[OSD([subQ0])]})]}),makeQuery(id+"F29.opExtrude","SWEPT_FACE",FACE,{"disambiguationData":[OSD([subQ5,subQ4,subQ3,subQ2,subQ1,subQ0])]})]})]});}
            var Q12;
            {var subQ0=sQuery(id+"F23.wireOp",EDGE,"E20");var subQ1=sQuery(id+"F15.wireOp",EDGE,"E16");var subQ2=sQuery(id+"F0.wireOp",EDGE,"E0.bottom");Q12=makeQuery(id+"F30.opChamfer","BLEND_EDGE",EDGE,{"blendedFrom":[makeQuery(id+"F27.opExtrude","CAP_EDGE",EDGE,{"disambiguationData":[OSD([subQ2,sQuery(id+"F2.wireOp",EDGE,"E2"),sQuery(id+"F2.wireOp",EDGE,"E4"),subQ1,sQuery(id+"F25.wireOp",EDGE,"E23")])],"isStart":false}),makeQuery(id+"F29.boolean.opBoolean","MERGE",FACE,{"derivedFrom":[makeQuery(id+"F27.boolean.opBoolean","MERGE",FACE,{"derivedFrom":[makeQuery(id+"F24.boolean.opBoolean","COPY",FACE,{"derivedFrom":makeQuery(id+"F24.opExtrude","SWEPT_FACE",FACE,{"disambiguationData":[OSD([subQ0])]})}),makeQuery(id+"F27.opExtrude","SWEPT_FACE",FACE,{"disambiguationData":[OSD([subQ0])]})]}),makeQuery(id+"F29.opExtrude","SWEPT_FACE",FACE,{"disambiguationData":[OSD([subQ2,sQuery(id+"F2.wireOp",EDGE,"E1"),sQuery(id+"F2.wireOp",EDGE,"E3"),sQuery(id+"F15.wireOp",EDGE,"E15"),subQ1,subQ0])]})]})],"blendedInto":[makeQuery(id+"F29.boolean.opBoolean","MERGE",FACE,{"derivedFrom":[makeQuery(id+"F27.boolean.opBoolean","MERGE",FACE,{"derivedFrom":[makeQuery(id+"F24.boolean.opBoolean","COPY",FACE,{"derivedFrom":makeQuery(id+"F24.opExtrude","SWEPT_FACE",FACE,{"disambiguationData":[OSD([subQ0])]})}),makeQuery(id+"F27.opExtrude","SWEPT_FACE",FACE,{"disambiguationData":[OSD([subQ0])]})]}),makeQuery(id+"F29.opExtrude","SWEPT_FACE",FACE,{"disambiguationData":[OSD([subQ2,sQuery(id+"F2.wireOp",EDGE,"E1"),sQuery(id+"F2.wireOp",EDGE,"E3"),sQuery(id+"F15.wireOp",EDGE,"E15"),subQ1,subQ0])]})]})]});}
            var Q13;
            {var subQ0=sQuery(id+"F13.wireOp",EDGE,"E14");var subQ1=sQuery(id+"F2.wireOp",EDGE,"E4");Q13=makeQuery(id+"F30.opChamfer","BLEND_EDGE",EDGE,{"blendedFrom":[makeQuery(id+"F27.opExtrude","CAP_EDGE",EDGE,{"disambiguationData":[OSD([sQuery(id+"F0.wireOp",EDGE,"E0.bottom"),sQuery(id+"F2.wireOp",EDGE,"E2"),subQ1,sQuery(id+"F15.wireOp",EDGE,"E16"),sQuery(id+"F25.wireOp",EDGE,"E23")])],"isStart":false}),makeQuery(id+"F29.boolean.opBoolean","MERGE",FACE,{"derivedFrom":[makeQuery(id+"F27.boolean.opBoolean","MERGE",FACE,{"derivedFrom":[makeQuery(id+"F14.boolean.opBoolean","COPY",FACE,{"derivedFrom":makeQuery(id+"F14.opExtrude","SWEPT_FACE",FACE,{"disambiguationData":[OSD([subQ0])]})}),makeQuery(id+"F27.opExtrude","SWEPT_FACE",FACE,{"disambiguationData":[OSD([subQ1,subQ0])]})]}),makeQuery(id+"F29.opExtrude","SWEPT_FACE",FACE,{"disambiguationData":[OSD([subQ0])]})]})],"blendedInto":[makeQuery(id+"F29.boolean.opBoolean","MERGE",FACE,{"derivedFrom":[makeQuery(id+"F27.boolean.opBoolean","MERGE",FACE,{"derivedFrom":[makeQuery(id+"F14.boolean.opBoolean","COPY",FACE,{"derivedFrom":makeQuery(id+"F14.opExtrude","SWEPT_FACE",FACE,{"disambiguationData":[OSD([subQ0])]})}),makeQuery(id+"F27.opExtrude","SWEPT_FACE",FACE,{"disambiguationData":[OSD([subQ1,subQ0])]})]}),makeQuery(id+"F29.opExtrude","SWEPT_FACE",FACE,{"disambiguationData":[OSD([subQ0])]})]})]});}
            var Q14;
            {var subQ0=sQuery(id+"F13.wireOp",EDGE,"E14");Q14=makeQuery(id+"F30.opChamfer","BLEND_EDGE",EDGE,{"blendedFrom":[makeQuery(id+"F29.opExtrude","CAP_EDGE",EDGE,{"disambiguationData":[OSD([sQuery(id+"F0.wireOp",EDGE,"E0.bottom"),sQuery(id+"F2.wireOp",EDGE,"E1"),sQuery(id+"F2.wireOp",EDGE,"E3"),sQuery(id+"F15.wireOp",EDGE,"E15"),sQuery(id+"F15.wireOp",EDGE,"E16"),sQuery(id+"F26.wireOp",EDGE,"E24")])],"isStart":false}),makeQuery(id+"F29.boolean.opBoolean","MERGE",FACE,{"derivedFrom":[makeQuery(id+"F27.boolean.opBoolean","MERGE",FACE,{"derivedFrom":[makeQuery(id+"F14.boolean.opBoolean","COPY",FACE,{"derivedFrom":makeQuery(id+"F14.opExtrude","SWEPT_FACE",FACE,{"disambiguationData":[OSD([subQ0])]})}),makeQuery(id+"F27.opExtrude","SWEPT_FACE",FACE,{"disambiguationData":[OSD([sQuery(id+"F2.wireOp",EDGE,"E4"),subQ0])]})]}),makeQuery(id+"F29.opExtrude","SWEPT_FACE",FACE,{"disambiguationData":[OSD([subQ0])]})]})],"blendedInto":[makeQuery(id+"F29.boolean.opBoolean","MERGE",FACE,{"derivedFrom":[makeQuery(id+"F27.boolean.opBoolean","MERGE",FACE,{"derivedFrom":[makeQuery(id+"F14.boolean.opBoolean","COPY",FACE,{"derivedFrom":makeQuery(id+"F14.opExtrude","SWEPT_FACE",FACE,{"disambiguationData":[OSD([subQ0])]})}),makeQuery(id+"F27.opExtrude","SWEPT_FACE",FACE,{"disambiguationData":[OSD([sQuery(id+"F2.wireOp",EDGE,"E4"),subQ0])]})]}),makeQuery(id+"F29.opExtrude","SWEPT_FACE",FACE,{"disambiguationData":[OSD([subQ0])]})]})]});}
            var Q15;
            Q15=makeQuery(id+"F27.opExtrude","CAP_EDGE",EDGE,{"disambiguationData":[OSD([sQuery(id+"F23.wireOp",EDGE,"E20")])],"isStart":false});
            fillet(context, id + "F31", {"entities" : qUnion([Q0, Q1, Q2, Q3, Q4, Q5, Q6, Q7, Q8, Q9, Q10, Q11, Q12, Q13, Q14, Q15]), "radius" : 1 * mm, "tangentPropagation" : true, "allowEdgeOverflow" : false});
        }
        {
            var Q0;
            Q0=qCreatedBy(makeId("Top.planeOp"),FACE);
            var sketch = newSketch(context, id + "F32", { "sketchPlane" : qUnion([Q0])});
            skLineSegment(sketch, "E25.bottom", {"start": v(35.75, 33.89) * mm, "end": v(-43.92, 33.89) * mm});
            skLineSegment(sketch, "E25.top", {"start": v(35.75, -36.42) * mm, "end": v(-43.92, -36.42) * mm});
            skLineSegment(sketch, "E25.left", {"start": v(35.75, 33.89) * mm, "end": v(35.75, -36.42) * mm});
            skLineSegment(sketch, "E25.right", {"start": v(-43.92, 33.89) * mm, "end": v(-43.92, -36.42) * mm});
            skSolve(sketch);
        }
        {
            var Q0;
            Q0 = qSketchRegion(id + "F32", true);
            var Q1;
            Q1=makeQuery(id+"F32.imprint","IMPRINT",FACE,{"disambiguationData":[TD([[makeQuery(id+"F32.imprint","IMPRINT",EDGE,{"derivedFrom":sQuery(id+"F32.wireOp",EDGE,"E25.bottom")}),1.0]])]});
            extrude(context, id + "F33", {"entities" : qUnion([Q0, Q1]), "oppositeDirection" : true, "depth" : 9.7 * mm, "offsetDistance" : 25 * mm});
        }
        {
            var Q0;
            Q0=makeQuery(id+"F33.opExtrude","SWEPT_BODY",BODY,{"disambiguationData":[OSD([sQuery(id+"F32.wireOp",EDGE,"E25.bottom"),sQuery(id+"F32.wireOp",EDGE,"E25.top"),sQuery(id+"F32.wireOp",EDGE,"E25.left"),sQuery(id+"F32.wireOp",EDGE,"E25.right")])]});
            transform(context, id + "F34", {"entities" : qUnion([Q0]), "transformType" : TransformType.TRANSLATION_3D, "dx" : 0 * mm, "dy" : 0 * mm, "dz" : 22.7 * mm, "makeCopy" : false});
        }
        {
            var Q0;
            Q0=makeQuery(id+"F33.opExtrude","SWEPT_BODY",BODY,{"disambiguationData":[OSD([sQuery(id+"F32.wireOp",EDGE,"E25.bottom"),sQuery(id+"F32.wireOp",EDGE,"E25.top"),sQuery(id+"F32.wireOp",EDGE,"E25.left"),sQuery(id+"F32.wireOp",EDGE,"E25.right")])]});
            var Q1;
            Q1=makeQuery(id+"F1.opExtrude","SWEPT_BODY",BODY,{"disambiguationData":[OSD([sQuery(id+"F0.wireOp",EDGE,"E0.bottom"),sQuery(id+"F0.wireOp",EDGE,"E0.top"),sQuery(id+"F0.wireOp",EDGE,"E0.left"),sQuery(id+"F0.wireOp",EDGE,"E0.right")])]});
            booleanBodies(context, id + "F35", {"operationType" : BooleanOperationType.SUBTRACTION, "tools" : qUnion([Q0]), "targets" : qUnion([Q1])});
        }
        {
            var Q0;
            Q0=makeQuery(id+"F1.opExtrude","SWEPT_BODY",BODY,{"disambiguationData":[OSD([sQuery(id+"F0.wireOp",EDGE,"E0.bottom"),sQuery(id+"F0.wireOp",EDGE,"E0.top"),sQuery(id+"F0.wireOp",EDGE,"E0.left"),sQuery(id+"F0.wireOp",EDGE,"E0.right")])]});
            transform(context, id + "F36", {"entities" : qUnion([Q0]), "transformType" : TransformType.TRANSLATION_3D, "dx" : 0 * mm, "dy" : -7.62 * mm, "dz" : 0 * mm, "makeCopy" : false});
        }
        {
            var Q0;
            Q0=makeQuery(id+"F1.opExtrude","SWEPT_BODY",BODY,{"disambiguationData":[OSD([sQuery(id+"F0.wireOp",EDGE,"E0.bottom"),sQuery(id+"F0.wireOp",EDGE,"E0.top"),sQuery(id+"F0.wireOp",EDGE,"E0.left"),sQuery(id+"F0.wireOp",EDGE,"E0.right")])]});
            transform(context, id + "F37", {"entities" : qUnion([Q0]), "transformType" : TransformType.TRANSLATION_3D, "dx" : 0 * mm, "dy" : -0.3 * mm, "dz" : 0 * mm, "makeCopy" : false});
        }
        {
            var Q0;
            {var subQ0=sQuery(id+"F23.wireOp",EDGE,"E21");Q0=makeQuery(id+"F29.boolean.opBoolean","MERGE",FACE,{"derivedFrom":[makeQuery(id+"F27.boolean.opBoolean","MERGE",FACE,{"derivedFrom":[makeQuery(id+"F24.boolean.opBoolean","COPY",FACE,{"derivedFrom":makeQuery(id+"F24.opExtrude","SWEPT_FACE",FACE,{"disambiguationData":[OSD([subQ0])]})}),makeQuery(id+"F27.opExtrude","SWEPT_FACE",FACE,{"disambiguationData":[OSD([subQ0])]})]}),makeQuery(id+"F29.opExtrude","SWEPT_FACE",FACE,{"disambiguationData":[OSD([sQuery(id+"F0.wireOp",EDGE,"E0.bottom"),sQuery(id+"F2.wireOp",EDGE,"E1"),sQuery(id+"F2.wireOp",EDGE,"E3"),sQuery(id+"F15.wireOp",EDGE,"E15"),sQuery(id+"F15.wireOp",EDGE,"E16"),subQ0])]})]});}
            var sketch = newSketch(context, id + "F38", { "sketchPlane" : qUnion([Q0])});
            skText(sketch, "E26", { "text": "AT", "fontName": "OpenSans-Regular.ttf"});
            const initialGuessF38  = {"E26": [-0.01476, 0.00745, 1, 0, 0.00407]};
            skSetInitialGuess(sketch, initialGuessF38);
            skSolve(sketch);
        }
        {
            var Q0;
            Q0 = qSketchRegion(id + "F38", true);
            extrude(context, id + "F39", {"entities" : qUnion([Q0]), "operationType" : NewBodyOperationType.REMOVE, "oppositeDirection" : true, "depth" : .4 * mm, "offsetDistance" : 25.4 * mm});
        }
    });
